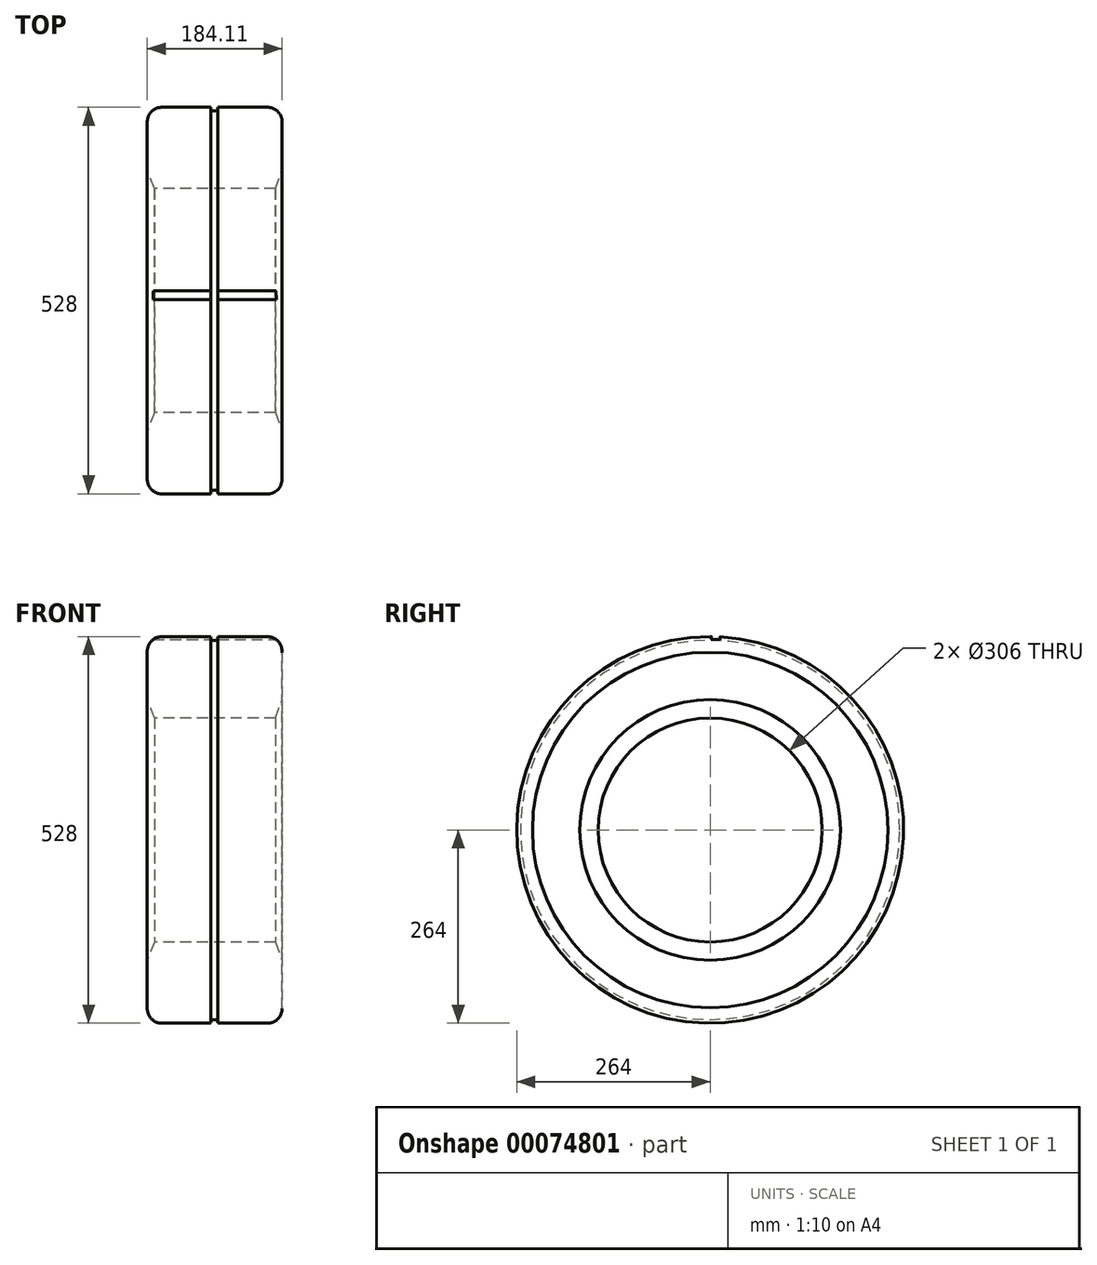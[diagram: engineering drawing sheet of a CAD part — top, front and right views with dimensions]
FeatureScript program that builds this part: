
annotation { "Feature Type Name" : "Feature", "Feature Type Description" : "" }
export const myFeature = defineFeature(function(context is Context, id is Id, definition is map)
    precondition{}
    {
        {
            var Q0;
            Q0=qCreatedBy(makeId("Front.planeOp"),FACE);
            var sketch = newSketch(context, id + "F0", { "sketchPlane" : qUnion([Q0])});
            skLineSegment(sketch, "E0", {"start": v(-276.1, 0) * mm, "end": v(269.09, 0) * mm, "construction": true});
            skLineSegment(sketch, "E1", {"start": v(-82.5, 153) * mm, "end": v(82.5, 153) * mm});
            skLineSegment(sketch, "E2", {"start": v(0, 0) * mm, "end": v(92.5, 153) * mm, "construction": true});
            skLineSegment(sketch, "E3", {"start": v(-72.5, 264) * mm, "end": v(-5.94, 264) * mm});
            skLineSegment(sketch, "E4", {"start": v(-92.5, 244) * mm, "end": v(-92.5, 178) * mm});
            skPoint(sketch, "E5.visualSharp", {"position": v(-92.5, 264) * mm});
            skArc(sketch, "E5.filletArc", {"start": v(-72.5, 264) * mm, "mid": v(-86.64, 258.14) * mm, "end": v(-92.5, 244) * mm});
            skPoint(sketch, "E6.visualSharp", {"position": v(92.5, 264) * mm});
            skArc(sketch, "E6.filletArc", {"start": v(91.56, 242.63) * mm, "mid": v(86.23, 257.65) * mm, "end": v(71.61, 264) * mm});
            skLineSegment(sketch, "E7", {"start": v(-82.5, 153) * mm, "end": v(-92.5, 178) * mm, "construction": true});
            skPoint(sketch, "E8.orphan", {"position": v(-92.5, 153) * mm});
            skPoint(sketch, "E9.end.orphan", {"position": v(91.56, 178) * mm});
            skLineSegment(sketch, "E10", {"start": v(91.56, 242.63) * mm, "end": v(91.56, 178) * mm});
            skLineSegment(sketch, "E11", {"start": v(91.56, 178) * mm, "end": v(82.5, 153) * mm});
            skLineSegment(sketch, "E12", {"start": v(-92.5, 178) * mm, "end": v(-82.5, 153) * mm});
            skLineSegment(sketch, "E13.top", {"start": v(4.06, 259) * mm, "end": v(-5.94, 259) * mm});
            skLineSegment(sketch, "E13.left", {"start": v(4.06, 264) * mm, "end": v(4.06, 259) * mm});
            skLineSegment(sketch, "E13.right", {"start": v(-5.94, 264) * mm, "end": v(-5.94, 259) * mm});
            skLineSegment(sketch, "E14.trimOffspring", {"start": v(4.06, 264) * mm, "end": v(71.61, 264) * mm});
            skSolve(sketch);
        }
        {
            var Q0;
            Q0 = qSketchRegion(id + "F0", true);
            var Q1;
            Q1=sQuery(id+"F0.wireOp",EDGE,"E0");
            revolve(context, id + "F1", {"entities" : qUnion([Q0]), "axis" : qUnion([Q1]), "revolveType" : RevolveType.FULL});
        }
        {
            var Q0;
            Q0=qCreatedBy(makeId("Top.planeOp"),FACE);
            cPlane(context, id + "F2", {"entities" : qUnion([Q0]), "cplaneType" : CPlaneType.OFFSET, "offset" : 260 * mm, "width" : 150 * mm, "height" : 150 * mm});
        }
        {
            var Q0;
            Q0=qCreatedBy(id+"F2.planeOp",FACE);
            var sketch = newSketch(context, id + "F3", { "sketchPlane" : qUnion([Q0])});
            skLineSegment(sketch, "E15.bottom", {"start": v(-111.23, 13.57) * mm, "end": v(113, 13.57) * mm});
            skLineSegment(sketch, "E15.top", {"start": v(-111.23, 1.57) * mm, "end": v(113, 1.57) * mm});
            skLineSegment(sketch, "E15.left", {"start": v(-111.23, 13.57) * mm, "end": v(-111.23, 1.57) * mm});
            skLineSegment(sketch, "E15.right", {"start": v(113, 13.57) * mm, "end": v(113, 1.57) * mm});
            skSolve(sketch);
        }
        {
            var Q0;
            Q0 = qSketchRegion(id + "F3", true);
            extrude(context, id + "F4", {"entities" : qUnion([Q0]), "operationType" : NewBodyOperationType.REMOVE, "depth" : 25 * mm});
        }
        {
            var Q0;
            Q0=makeQuery(id+"F1.opRevolve","SWEPT_BODY",BODY,{"disambiguationData":[OSD([sQuery(id+"F0.wireOp",EDGE,"E1"),sQuery(id+"F0.wireOp",EDGE,"E3"),sQuery(id+"F0.wireOp",EDGE,"E4"),sQuery(id+"F0.wireOp",EDGE,"E5.filletArc"),sQuery(id+"F0.wireOp",EDGE,"E6.filletArc"),sQuery(id+"F0.wireOp",EDGE,"E10"),sQuery(id+"F0.wireOp",EDGE,"E11"),sQuery(id+"F0.wireOp",EDGE,"E12"),sQuery(id+"F0.wireOp",EDGE,"E13.top"),sQuery(id+"F0.wireOp",EDGE,"E13.left"),sQuery(id+"F0.wireOp",EDGE,"E13.right"),sQuery(id+"F0.wireOp",EDGE,"E14.trimOffspring")])]});
            transform(context, id + "F5", {"entities" : qUnion([Q0]), "transformType" : TransformType.TRANSLATION_3D, "dx" : 0 * mm, "dy" : 0 * mm, "dz" : 0 * mm, "makeCopy" : true});
        }
    });
